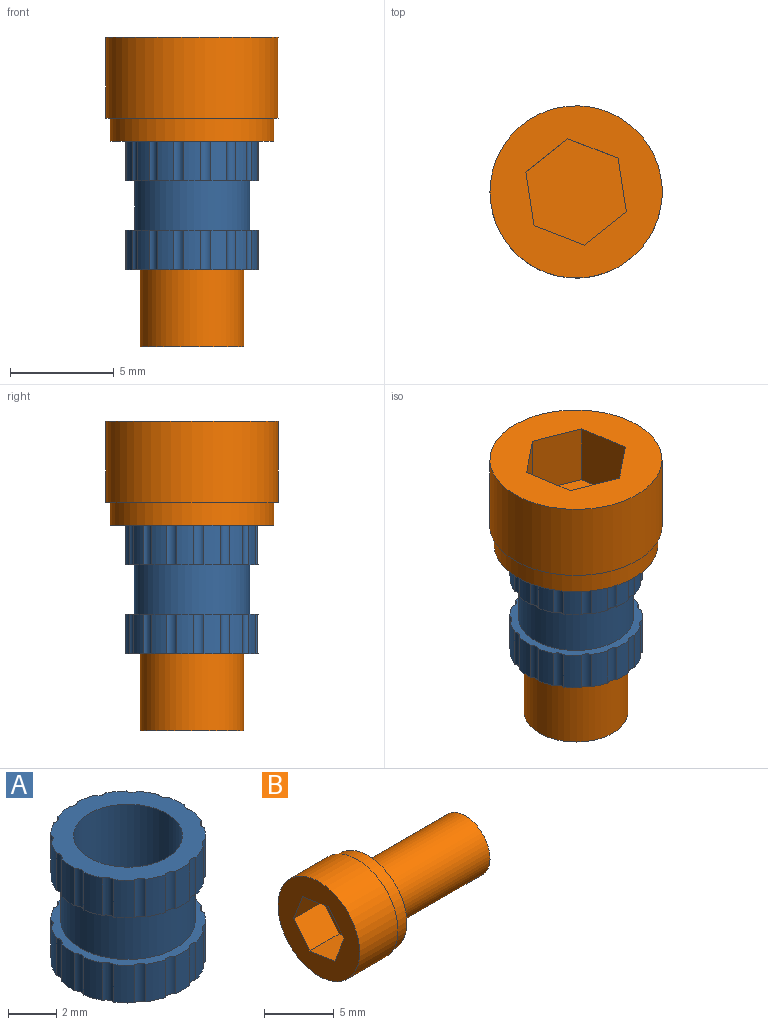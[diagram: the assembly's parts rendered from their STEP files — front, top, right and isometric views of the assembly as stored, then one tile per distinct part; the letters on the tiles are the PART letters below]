
ASSEMBLY  parts=2 mates=1
PART A: 66 faces, bbox 6.4x6.4x6.2 mm
  f0: cylinder r=3.2mm len=1.9mm, axis (0,0,-1), area 1.6mm2, adj f2,f57,f59,f65
  f1: cylinder r=3.2mm len=1.9mm, axis (0,0,-1), area 1.6mm2, adj f3,f61,f63,f64
  f2: cylinder r=0.38mm len=1.9mm, axis (0,0,1), area 1mm2, adj f0,f4,f57,f59
  f3: cylinder r=0.38mm len=1.9mm, axis (0,0,1), area 1mm2, adj f1,f5,f61,f63
  f4: cylinder r=3.2mm len=1.9mm, axis (0,0,-1), area 1.6mm2, adj f2,f6,f57,f59
  f5: cylinder r=3.2mm len=1.9mm, axis (0,0,-1), area 1.6mm2, adj f3,f7,f61,f63
  f6: cylinder r=0.38mm len=1.9mm, axis (0,0,1), area 1mm2, adj f4,f8,f57,f59
  f7: cylinder r=0.38mm len=1.9mm, axis (0,0,1), area 1mm2, adj f5,f9,f61,f63
  f8: cylinder r=3.2mm len=1.9mm, axis (0,0,-1), area 1.6mm2, adj f6,f10,f57,f59
  f9: cylinder r=3.2mm len=1.9mm, axis (0,0,-1), area 1.6mm2, adj f7,f11,f61,f63
  f10: cylinder r=0.38mm len=1.9mm, axis (0,0,1), area 1mm2, adj f8,f12,f57,f59
  f11: cylinder r=0.38mm len=1.9mm, axis (0,0,1), area 1mm2, adj f9,f13,f61,f63
  f12: cylinder r=3.2mm len=1.9mm, axis (0,0,-1), area 1.6mm2, adj f10,f14,f57,f59
  f13: cylinder r=3.2mm len=1.9mm, axis (0,0,-1), area 1.6mm2, adj f11,f15,f61,f63
  f14: cylinder r=0.38mm len=1.9mm, axis (0,0,1), area 1mm2, adj f12,f16,f57,f59
  f15: cylinder r=0.38mm len=1.9mm, axis (0,0,1), area 1mm2, adj f13,f17,f61,f63
  f16: cylinder r=3.2mm len=1.9mm, axis (0,0,-1), area 1.6mm2, adj f14,f18,f57,f59
  f17: cylinder r=3.2mm len=1.9mm, axis (0,0,-1), area 1.6mm2, adj f15,f19,f61,f63
  f18: cylinder r=0.38mm len=1.9mm, axis (0,0,1), area 1mm2, adj f16,f20,f57,f59
  f19: cylinder r=0.38mm len=1.9mm, axis (0,0,1), area 1mm2, adj f17,f21,f61,f63
  f20: cylinder r=3.2mm len=1.9mm, axis (0,0,-1), area 1.6mm2, adj f18,f22,f57,f59
  f21: cylinder r=3.2mm len=1.9mm, axis (0,0,-1), area 1.6mm2, adj f19,f23,f61,f63
  f22: cylinder r=0.38mm len=1.9mm, axis (0,0,1), area 1mm2, adj f20,f24,f57,f59
  f23: cylinder r=0.38mm len=1.9mm, axis (0,0,1), area 1mm2, adj f21,f25,f61,f63
  f24: cylinder r=3.2mm len=1.9mm, axis (0,0,-1), area 1.6mm2, adj f22,f26,f57,f59
  f25: cylinder r=3.2mm len=1.9mm, axis (0,0,-1), area 1.6mm2, adj f23,f27,f61,f63
  f26: cylinder r=0.38mm len=1.9mm, axis (0,0,1), area 1mm2, adj f24,f28,f57,f59
  f27: cylinder r=0.38mm len=1.9mm, axis (0,0,1), area 1mm2, adj f25,f29,f61,f63
  f28: cylinder r=3.2mm len=1.9mm, axis (0,0,-1), area 1.6mm2, adj f26,f30,f57,f59
  f29: cylinder r=3.2mm len=1.9mm, axis (0,0,-1), area 1.6mm2, adj f27,f31,f61,f63
  f30: cylinder r=0.38mm len=1.9mm, axis (0,0,1), area 1mm2, adj f28,f32,f57,f59
  f31: cylinder r=0.38mm len=1.9mm, axis (0,0,1), area 1mm2, adj f29,f33,f61,f63
  f32: cylinder r=3.2mm len=1.9mm, axis (0,0,-1), area 1.6mm2, adj f30,f34,f57,f59
  f33: cylinder r=3.2mm len=1.9mm, axis (0,0,-1), area 1.6mm2, adj f31,f35,f61,f63
  f34: cylinder r=0.38mm len=1.9mm, axis (0,0,1), area 1mm2, adj f32,f36,f57,f59
  f35: cylinder r=0.38mm len=1.9mm, axis (0,0,1), area 1mm2, adj f33,f37,f61,f63
  f36: cylinder r=3.2mm len=1.9mm, axis (0,0,-1), area 1.6mm2, adj f34,f38,f57,f59
  f37: cylinder r=3.2mm len=1.9mm, axis (0,0,-1), area 1.6mm2, adj f35,f39,f61,f63
  f38: cylinder r=0.38mm len=1.9mm, axis (0,0,1), area 1mm2, adj f36,f40,f57,f59
  f39: cylinder r=0.38mm len=1.9mm, axis (0,0,1), area 1mm2, adj f37,f41,f61,f63
  f40: cylinder r=3.2mm len=1.9mm, axis (0,0,-1), area 1.6mm2, adj f38,f42,f57,f59
  f41: cylinder r=3.2mm len=1.9mm, axis (0,0,-1), area 1.6mm2, adj f39,f43,f61,f63
  f42: cylinder r=0.38mm len=1.9mm, axis (0,0,1), area 1mm2, adj f40,f44,f57,f59
  f43: cylinder r=0.38mm len=1.9mm, axis (0,0,1), area 1mm2, adj f41,f45,f61,f63
  f44: cylinder r=3.2mm len=1.9mm, axis (0,0,-1), area 1.6mm2, adj f42,f46,f57,f59
  f45: cylinder r=3.2mm len=1.9mm, axis (0,0,-1), area 1.6mm2, adj f43,f47,f61,f63
  f46: cylinder r=0.38mm len=1.9mm, axis (0,0,1), area 1mm2, adj f44,f48,f57,f59
  f47: cylinder r=0.38mm len=1.9mm, axis (0,0,1), area 1mm2, adj f45,f49,f61,f63
  f48: cylinder r=3.2mm len=1.9mm, axis (0,0,-1), area 1.6mm2, adj f46,f50,f57,f59
  f49: cylinder r=3.2mm len=1.9mm, axis (0,0,-1), area 1.6mm2, adj f47,f51,f61,f63
  f50: cylinder r=0.38mm len=1.9mm, axis (0,0,1), area 1mm2, adj f48,f52,f57,f59
  f51: cylinder r=0.38mm len=1.9mm, axis (0,0,1), area 1mm2, adj f49,f53,f61,f63
  f52: cylinder r=3.2mm len=1.9mm, axis (0,0,-1), area 1.6mm2, adj f50,f54,f57,f59
  f53: cylinder r=3.2mm len=1.9mm, axis (0,0,-1), area 1.6mm2, adj f51,f55,f61,f63
  f54: cylinder r=0.38mm len=1.9mm, axis (0,0,1), area 1mm2, adj f52,f57,f58,f59
  f55: cylinder r=0.38mm len=1.9mm, axis (0,0,1), area 1mm2, adj f53,f61,f62,f63
  f56: cylinder r=2.25mm len=6.2mm, axis (0,0,-1), area 87.7mm2, adj f57,f63
  f57: plane 6.4x6.39mm, normal (0,0,-1), area 15.8mm2, adj f0,f2,f4,f6,f8,f10,f12,f14
  f58: cylinder r=3.2mm len=1.9mm, axis (0,0,-1), area 1.6mm2, adj f54,f57,f59,f65
  f59: plane 6.4x6.39mm, normal (0,0,1), area 7.5mm2, adj f0,f2,f4,f6,f8,f10,f12,f14
  f60: cylinder r=2.77mm len=5.55mm, axis (0,0,-1), area 41.8mm2, adj f59,f61
  f61: plane 6.4x6.39mm, normal (0,0,-1), area 7.5mm2, adj f1,f3,f5,f7,f9,f11,f13,f15
  f62: cylinder r=3.2mm len=1.9mm, axis (0,0,-1), area 1.6mm2, adj f55,f61,f63,f64
  f63: plane 6.4x6.39mm, normal (0,0,1), area 15.8mm2, adj f1,f3,f5,f7,f9,f11,f13,f15
  f64: cylinder r=0.38mm len=1.9mm, axis (0,0,1), area 1mm2, adj f1,f61,f62,f63
  f65: cylinder r=0.38mm len=1.9mm, axis (0,0,1), area 1mm2, adj f0,f57,f58,f59
PART B: 14 faces, bbox 14.9x8.3x8.3 mm
  f0: cylinder r=2.5mm len=9.9mm, axis (-1,0,0), area 155.5mm2, adj f1,f3
  f1: plane 5x5mm, normal (1,0,0), area 19.6mm2, adj f0
  f2: plane 8.3x8.3mm, normal (-1,0,0), area 36.6mm2, adj f6,f7,f8,f9,f10,f11,f12
  f3: plane 7.9x7.9mm, normal (1,0,0), area 29.4mm2, adj f0,f4
  f4: cylinder r=3.95mm len=7.9mm, axis (1,0,0), area 27.3mm2, adj f3,f5
  f5: plane 8.3x8.3mm, normal (1,0,0), area 5.1mm2, adj f4,f6
  f6: cylinder r=4.15mm len=8.3mm, axis (1,0,0), area 101.7mm2, adj f2,f5
  f7: plane 3x2.57mm, normal (0,0.15,0.99), area 7.8mm2, adj f2,f8,f12,f13
  f8: plane 3x2.42mm, normal (0,0.93,0.36), area 7.8mm2, adj f2,f7,f9,f13
  f9: plane 3x2.03mm, normal (0,0.78,-0.63), area 7.8mm2, adj f2,f8,f10,f13
  f10: plane 3x2.57mm, normal (0,-0.15,-0.99), area 7.8mm2, adj f2,f9,f11,f13
  f11: plane 3x2.42mm, normal (0,-0.93,-0.36), area 7.8mm2, adj f2,f10,f12,f13
  f12: plane 3x2.03mm, normal (0,-0.78,0.63), area 7.8mm2, adj f2,f7,f11,f13
  f13: plane 5.14x4.84mm, normal (-1,0,0), area 17.5mm2, adj f7,f8,f9,f10,f11,f12
PLACE A t=(6.53,9.41,2.05)mm fixed
PLACE B rot(axis=(0,1,0),90deg) t=(6.53,9.41,8.25)mm
MATE fastened B.f0 <-> A.f0  axis (0,0,1) through (6.53,9.41,8.25)mm
